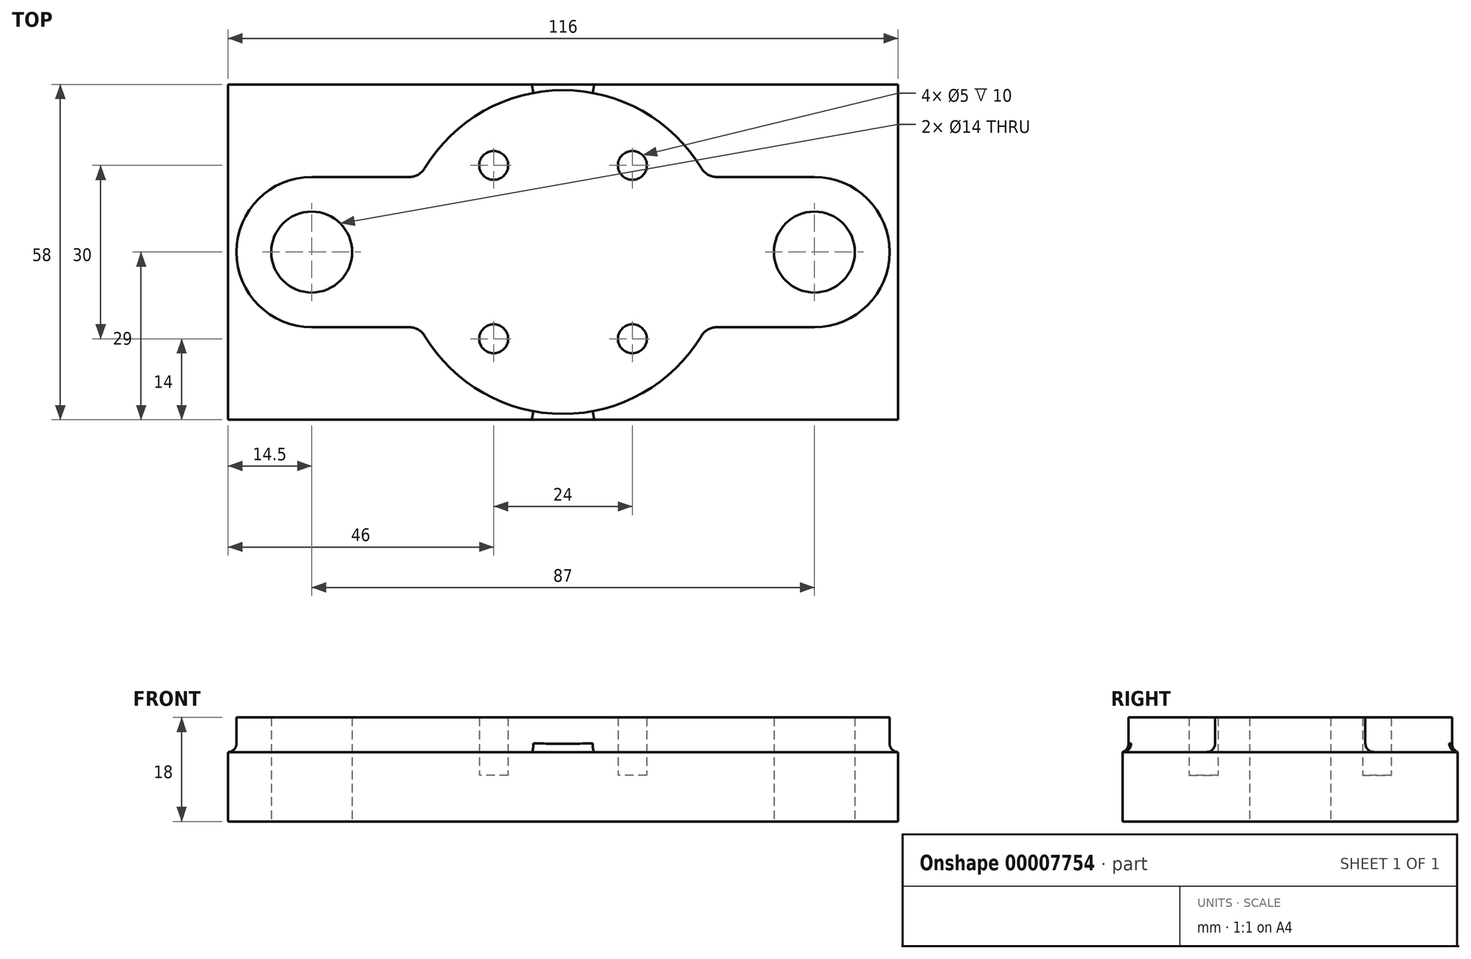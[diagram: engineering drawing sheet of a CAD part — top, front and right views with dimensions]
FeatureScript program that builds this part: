
annotation { "Feature Type Name" : "Feature", "Feature Type Description" : "" }
export const myFeature = defineFeature(function(context is Context, id is Id, definition is map)
    precondition{}
    {
        {
            var Q0;
            Q0=qCreatedBy(makeId("Top.planeOp"),FACE);
            var sketch = newSketch(context, id + "F0", { "sketchPlane" : qUnion([Q0])});
            skLineSegment(sketch, "E0.rect.bottom", {"start": v(-58, -29) * mm, "end": v(58, -29) * mm});
            skLineSegment(sketch, "E0.rect.top", {"start": v(-58, 29) * mm, "end": v(58, 29) * mm});
            skLineSegment(sketch, "E0.rect.left", {"start": v(-58, -29) * mm, "end": v(-58, 29) * mm});
            skLineSegment(sketch, "E0.rect.right", {"start": v(58, -29) * mm, "end": v(58, 29) * mm});
            skPoint(sketch, "E0.rect.middle", {"position": v(0, 0) * mm});
            skSolve(sketch);
        }
        {
            var Q0;
            Q0 = qSketchRegion(id + "F0", true);
            extrude(context, id + "F1", {"entities" : qUnion([Q0]), "depth" : 12 * mm});
        }
        {
            var Q0;
            Q0=makeQuery(id+"F1.opExtrude","CAP_FACE",FACE,{"disambiguationData":[OSD([sQuery(id+"F0.wireOp",EDGE,"E0.rect.bottom"),sQuery(id+"F0.wireOp",EDGE,"E0.rect.top"),sQuery(id+"F0.wireOp",EDGE,"E0.rect.left"),sQuery(id+"F0.wireOp",EDGE,"E0.rect.right")])],"isStart":false});
            var sketch = newSketch(context, id + "F2", { "sketchPlane" : qUnion([Q0])});
            skCircle(sketch, "E1", {"center": v(-43.5, 0) * mm, "radius": 7 * mm});
            skCircle(sketch, "E2", {"center": v(43.5, 0) * mm, "radius": 7 * mm});
            skLineSegment(sketch, "E3", {"start": v(0, 29) * mm, "end": v(0, -29) * mm, "construction": true});
            skArc(sketch, "E4", {"start": v(43.5, -13) * mm, "mid": v(56.5, 0) * mm, "end": v(43.5, 13) * mm});
            skArc(sketch, "E5", {"start": v(-43.5, 13) * mm, "mid": v(-56.5, 0) * mm, "end": v(-43.5, -13) * mm});
            skArc(sketch, "E6", {"start": v(23.98, 14.45) * mm, "mid": v(0, 28) * mm, "end": v(-23.98, 14.45) * mm});
            skLineSegment(sketch, "E7", {"start": v(-43.5, 13) * mm, "end": v(-26.55, 13) * mm});
            skLineSegment(sketch, "E8", {"start": v(26.55, 13) * mm, "end": v(43.5, 13) * mm});
            skLineSegment(sketch, "E9", {"start": v(-43.5, 0) * mm, "end": v(43.5, 0) * mm, "construction": true});
            skLineSegment(sketch, "E10.0.MirrorCS", {"start": v(-43.5, -13) * mm, "end": v(-26.55, -13) * mm});
            skArc(sketch, "E11.0.MirrorCS", {"start": v(23.98, -14.45) * mm, "mid": v(0, -28) * mm, "end": v(-23.98, -14.45) * mm});
            skLineSegment(sketch, "E12.0.MirrorCS", {"start": v(26.55, -13) * mm, "end": v(43.5, -13) * mm});
            skCircle(sketch, "E13", {"center": v(-12, 15) * mm, "radius": 2.5 * mm});
            skCircle(sketch, "E14.0.1.0", {"center": v(-12, -15) * mm, "radius": 2.5 * mm});
            skCircle(sketch, "E14.1.0.0", {"center": v(12, 15) * mm, "radius": 2.5 * mm});
            skCircle(sketch, "E14.1.1.0", {"center": v(12, -15) * mm, "radius": 2.5 * mm});
            skLineSegment(sketch, "E14.direction1", {"start": v(-12, 15) * mm, "end": v(12, 15) * mm, "construction": true});
            skLineSegment(sketch, "E14.direction2", {"start": v(-12, 15) * mm, "end": v(-12, -15) * mm, "construction": true});
            skPoint(sketch, "E15.visualSharp", {"position": v(-24.8, 13) * mm});
            skArc(sketch, "E15.filletArc", {"start": v(-26.55, 13) * mm, "mid": v(-25.08, 13.39) * mm, "end": v(-23.98, 14.45) * mm});
            skPoint(sketch, "E16.visualSharp", {"position": v(-24.8, -13) * mm});
            skArc(sketch, "E16.filletArc", {"start": v(-23.98, -14.45) * mm, "mid": v(-25.08, -13.39) * mm, "end": v(-26.55, -13) * mm});
            skPoint(sketch, "E17.visualSharp", {"position": v(24.8, 13) * mm});
            skArc(sketch, "E17.filletArc", {"start": v(23.98, 14.45) * mm, "mid": v(25.08, 13.39) * mm, "end": v(26.55, 13) * mm});
            skPoint(sketch, "E18.visualSharp", {"position": v(24.8, -13) * mm});
            skArc(sketch, "E18.filletArc", {"start": v(26.55, -13) * mm, "mid": v(25.08, -13.39) * mm, "end": v(23.98, -14.45) * mm});
            skSolve(sketch);
        }
        {
            var Q0;
            Q0 = qSketchRegion(id + "F2", true);
            extrude(context, id + "F3", {"entities" : qUnion([Q0]), "operationType" : NewBodyOperationType.ADD, "depth" : 6 * mm});
        }
        {
            var Q0;
            Q0=makeQuery(id+"F3.boolean.opBoolean","SPLIT",FACE,{"disambiguationData":[TD([makeQuery(id+"F3.opExtrude","SWEPT_FACE",FACE,{"disambiguationData":[OSD([sQuery(id+"F2.wireOp",EDGE,"E1")])]})])],"derivedFrom":makeQuery(id+"F1.opExtrude","CAP_FACE",FACE,{"disambiguationData":[OSD([sQuery(id+"F0.wireOp",EDGE,"E0.rect.bottom"),sQuery(id+"F0.wireOp",EDGE,"E0.rect.top"),sQuery(id+"F0.wireOp",EDGE,"E0.rect.left"),sQuery(id+"F0.wireOp",EDGE,"E0.rect.right")])],"isStart":false})});
            var sketch = newSketch(context, id + "F4", { "sketchPlane" : qUnion([Q0])});
            skCircle(sketch, "E19.1.0", {"center": v(43.5, 0) * mm, "radius": 7 * mm});
            skCircle(sketch, "E20.0", {"center": v(-43.5, 0) * mm, "radius": 7 * mm});
            skSolve(sketch);
        }
        {
            var Q0;
            Q0 = qSketchRegion(id + "F4", true);
            extrude(context, id + "F5", {"entities" : qUnion([Q0]), "operationType" : NewBodyOperationType.REMOVE, "endBound" : BoundingType.THROUGH_ALL, "oppositeDirection" : true, "depth" : 25 * mm});
        }
        {
            var Q0;
            Q0=makeQuery(id+"F3.boolean.opBoolean","SPLIT",FACE,{"disambiguationData":[TD([makeQuery(id+"F3.opExtrude","SWEPT_FACE",FACE,{"disambiguationData":[OSD([sQuery(id+"F2.wireOp",EDGE,"E14.0.1.0")])]})])],"derivedFrom":makeQuery(id+"F1.opExtrude","CAP_FACE",FACE,{"disambiguationData":[OSD([sQuery(id+"F0.wireOp",EDGE,"E0.rect.bottom"),sQuery(id+"F0.wireOp",EDGE,"E0.rect.top"),sQuery(id+"F0.wireOp",EDGE,"E0.rect.left"),sQuery(id+"F0.wireOp",EDGE,"E0.rect.right")])],"isStart":false})});
            var sketch = newSketch(context, id + "F6", { "sketchPlane" : qUnion([Q0])});
            skCircle(sketch, "E21.0", {"center": v(-12, -15) * mm, "radius": 2.5 * mm});
            skCircle(sketch, "E21.1", {"center": v(-12, 15) * mm, "radius": 2.5 * mm});
            skCircle(sketch, "E21.2", {"center": v(12, 15) * mm, "radius": 2.5 * mm});
            skCircle(sketch, "E21.3", {"center": v(12, -15) * mm, "radius": 2.5 * mm});
            skSolve(sketch);
        }
        {
            var Q0;
            Q0 = qSketchRegion(id + "F6", true);
            extrude(context, id + "F7", {"entities" : qUnion([Q0]), "operationType" : NewBodyOperationType.REMOVE, "oppositeDirection" : true, "depth" : 4 * mm});
        }
        {
            var Q0;
            Q0=makeQuery(id+"F3.opExtrude","CAP_EDGE",EDGE,{"disambiguationData":[OSD([sQuery(id+"F2.wireOp",EDGE,"E5")])],"isStart":true});
            fillet(context, id + "F8", {"entities" : qUnion([Q0]), "radius" : 1.5 * mm, "tangentPropagation" : true, "allowEdgeOverflow" : false});
        }
    });
